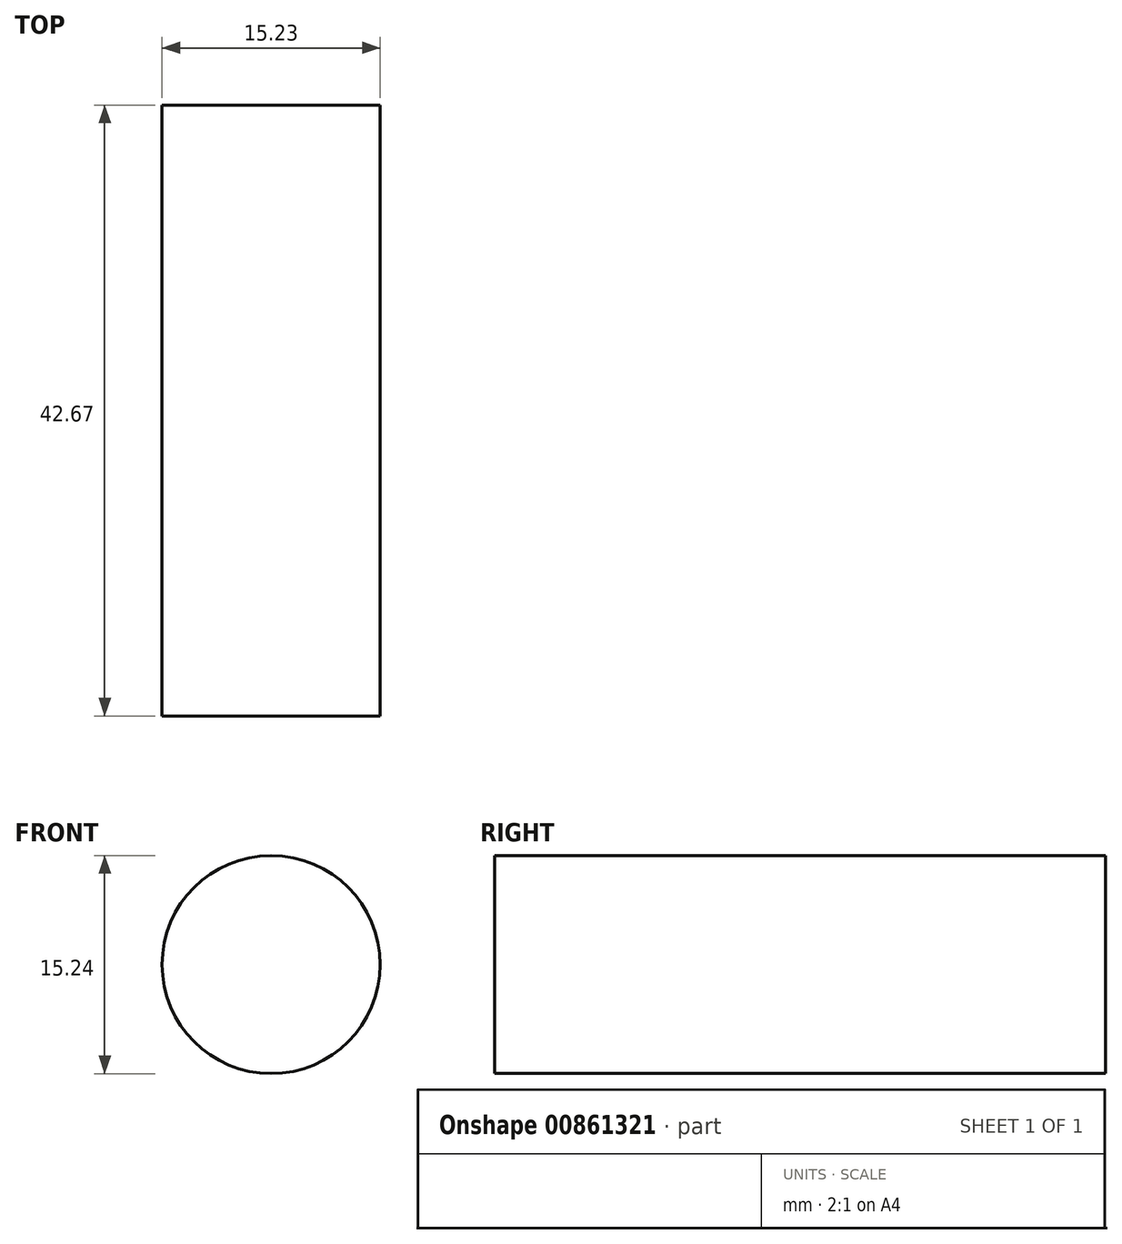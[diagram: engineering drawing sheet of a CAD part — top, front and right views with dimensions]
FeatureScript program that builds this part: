
annotation { "Feature Type Name" : "Feature", "Feature Type Description" : "" }
export const myFeature = defineFeature(function(context is Context, id is Id, definition is map)
    precondition{}
    {
        {
            var Q0;
            Q0=qCreatedBy(makeId("Front.planeOp"),FACE);
            var sketch = newSketch(context, id + "F0", { "sketchPlane" : qUnion([Q0])});
            skCircle(sketch, "E0", {"center": v(-16.61, 16.5) * mm, "radius": 7.62 * mm});
            skSolve(sketch);
        }
        {
            var Q0;
            Q0=makeQuery(id+"F0.imprint","IMPRINT",FACE,{"disambiguationData":[TD([[makeQuery(id+"F0.imprint","IMPRINT",EDGE,{"derivedFrom":sQuery(id+"F0.wireOp",EDGE,"E0")}),1.0]])]});
            extrude(context, id + "F1", {"entities" : qUnion([Q0]), "depth" : 42.67 * mm, "offsetDistance" : 25.4 * mm});
        }
    });
